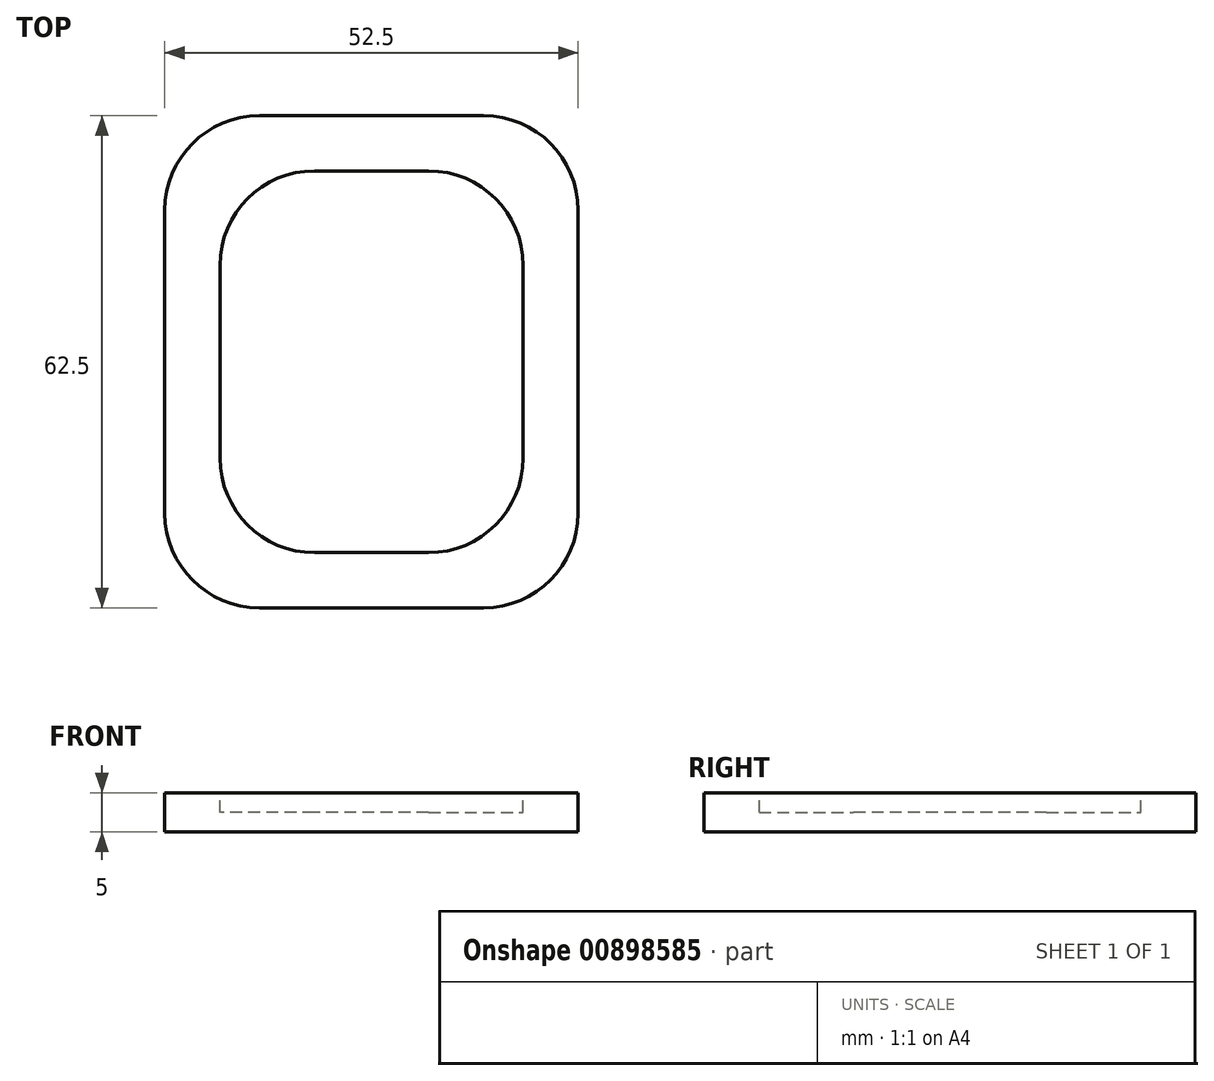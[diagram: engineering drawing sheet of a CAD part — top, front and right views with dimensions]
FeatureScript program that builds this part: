
annotation { "Feature Type Name" : "Feature", "Feature Type Description" : "" }
export const myFeature = defineFeature(function(context is Context, id is Id, definition is map)
    precondition{}
    {
        {
            var Q0;
            Q0=qCreatedBy(makeId("Top.planeOp"),FACE);
            var sketch = newSketch(context, id + "F0", { "sketchPlane" : qUnion([Q0])});
            skLineSegment(sketch, "E0.bottom", {"start": v(12, 0) * mm, "end": v(40.5, 0) * mm});
            skLineSegment(sketch, "E0.top", {"start": v(12, -62.5) * mm, "end": v(40.5, -62.5) * mm});
            skLineSegment(sketch, "E0.left", {"start": v(0, -12) * mm, "end": v(0, -50.5) * mm});
            skLineSegment(sketch, "E0.right", {"start": v(52.5, -12) * mm, "end": v(52.5, -50.5) * mm});
            skPoint(sketch, "E1.visualSharp", {"position": v(0, 0) * mm});
            skArc(sketch, "E1.filletArc", {"start": v(12, 0) * mm, "mid": v(3.51, -3.51) * mm, "end": v(0, -12) * mm});
            skPoint(sketch, "E2.visualSharp", {"position": v(52.5, 0) * mm});
            skArc(sketch, "E2.filletArc", {"start": v(52.5, -12) * mm, "mid": v(48.99, -3.51) * mm, "end": v(40.5, 0) * mm});
            skPoint(sketch, "E3.visualSharp", {"position": v(0, -62.5) * mm});
            skArc(sketch, "E3.filletArc", {"start": v(0, -50.5) * mm, "mid": v(3.51, -58.99) * mm, "end": v(12, -62.5) * mm});
            skPoint(sketch, "E4.visualSharp", {"position": v(52.5, -62.5) * mm});
            skArc(sketch, "E4.filletArc", {"start": v(40.5, -62.5) * mm, "mid": v(48.99, -58.99) * mm, "end": v(52.5, -50.5) * mm});
            skSolve(sketch);
        }
        {
            var Q0;
            Q0 = qSketchRegion(id + "F0", true);
            extrude(context, id + "F1", {"entities" : qUnion([Q0]), "depth" : 5 * mm, "offsetDistance" : 25 * mm});
        }
        {
            var Q0;
            Q0=makeQuery(id+"F1.opExtrude","CAP_FACE",FACE,{"disambiguationData":[OSD([sQuery(id+"F0.wireOp",EDGE,"E0.bottom"),sQuery(id+"F0.wireOp",EDGE,"E0.top"),sQuery(id+"F0.wireOp",EDGE,"E0.left"),sQuery(id+"F0.wireOp",EDGE,"E0.right"),sQuery(id+"F0.wireOp",EDGE,"E1.filletArc"),sQuery(id+"F0.wireOp",EDGE,"E2.filletArc"),sQuery(id+"F0.wireOp",EDGE,"E3.filletArc"),sQuery(id+"F0.wireOp",EDGE,"E4.filletArc")])],"isStart":false});
            var sketch = newSketch(context, id + "F2", { "sketchPlane" : qUnion([Q0])});
            skPoint(sketch, "E5", {"position": v(26.25, -31.25) * mm});
            skPoint(sketch, "E5.positionSnap0", {"position": v(52.44, -31.25) * mm});
            skPoint(sketch, "E5.positionSnap1", {"position": v(26.25, -0.3) * mm});
            skLineSegment(sketch, "E6.bottom", {"start": v(45.5, -7) * mm, "end": v(7, -7) * mm});
            skLineSegment(sketch, "E6.top", {"start": v(45.5, -55.5) * mm, "end": v(7, -55.5) * mm});
            skLineSegment(sketch, "E6.left", {"start": v(45.5, -7) * mm, "end": v(45.5, -55.5) * mm});
            skLineSegment(sketch, "E6.right", {"start": v(7, -7) * mm, "end": v(7, -55.5) * mm});
            skSolve(sketch);
        }
        {
            var Q0;
            Q0 = qSketchRegion(id + "F2", true);
            extrude(context, id + "F3", {"entities" : qUnion([Q0]), "operationType" : NewBodyOperationType.REMOVE, "oppositeDirection" : true, "depth" : 2.5 * mm, "offsetDistance" : 25 * mm});
        }
        {
            var Q0;
            Q0=makeQuery(id+"F3.boolean.opBoolean","COPY",EDGE,{"derivedFrom":makeQuery(id+"F3.opExtrude","SWEPT_EDGE",EDGE,{"disambiguationData":[OSD([sQuery(id+"F2.wireOp",EDGE,"E6.bottom"),sQuery(id+"F2.wireOp",EDGE,"E6.right")])]})});
            var Q1;
            Q1=makeQuery(id+"F3.boolean.opBoolean","COPY",EDGE,{"derivedFrom":makeQuery(id+"F3.opExtrude","SWEPT_EDGE",EDGE,{"disambiguationData":[OSD([sQuery(id+"F2.wireOp",EDGE,"E6.bottom"),sQuery(id+"F2.wireOp",EDGE,"E6.left")])]})});
            var Q2;
            Q2=makeQuery(id+"F3.boolean.opBoolean","COPY",EDGE,{"derivedFrom":makeQuery(id+"F3.opExtrude","SWEPT_EDGE",EDGE,{"disambiguationData":[OSD([sQuery(id+"F2.wireOp",EDGE,"E6.top"),sQuery(id+"F2.wireOp",EDGE,"E6.right")])]})});
            var Q3;
            Q3=makeQuery(id+"F3.boolean.opBoolean","COPY",EDGE,{"derivedFrom":makeQuery(id+"F3.opExtrude","SWEPT_EDGE",EDGE,{"disambiguationData":[OSD([sQuery(id+"F2.wireOp",EDGE,"E6.top"),sQuery(id+"F2.wireOp",EDGE,"E6.left")])]})});
            fillet(context, id + "F4", {"entities" : qUnion([Q0, Q1, Q2, Q3]), "radius" : 12 * mm, "tangentPropagation" : true, "allowEdgeOverflow" : false});
        }
    });
